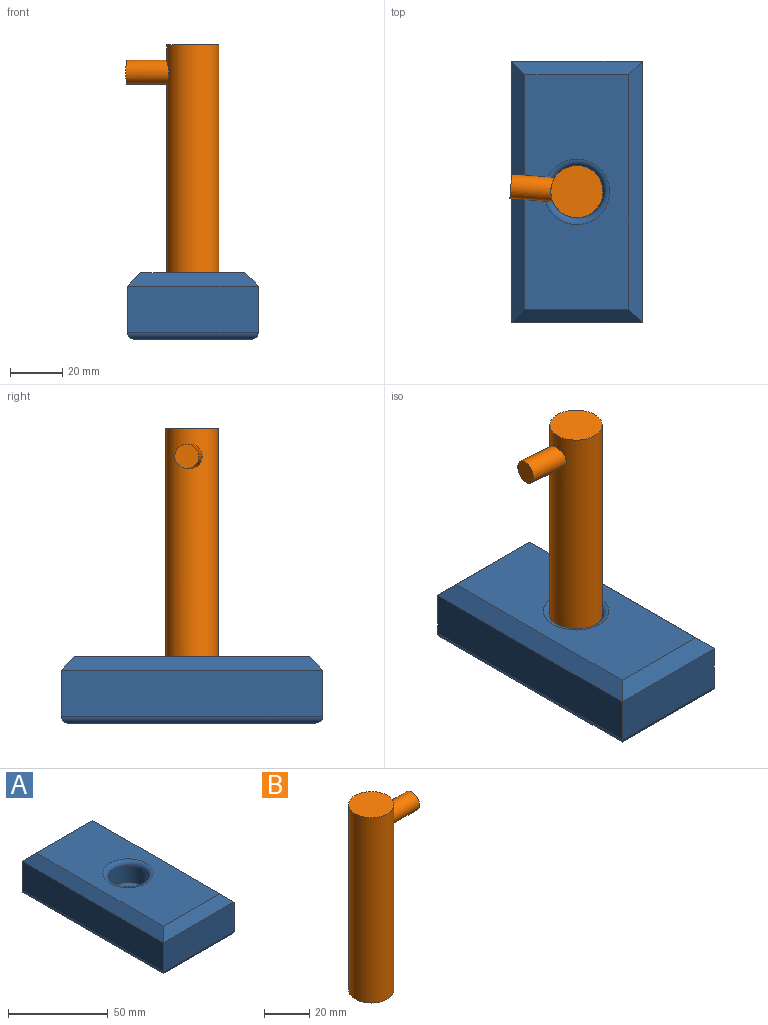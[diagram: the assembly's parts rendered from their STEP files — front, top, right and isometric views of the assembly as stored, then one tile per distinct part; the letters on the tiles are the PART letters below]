
ASSEMBLY  parts=2 mates=1
PART A: 17 faces, bbox 50x100x25.4 mm
  f0: plane 100x17.78mm, normal (1,0,0), area 1778mm2, adj f1,f3,f6,f13
  f1: plane 50x17.78mm, normal (0,1,0), area 889mm2, adj f0,f2,f8,f15
  f2: plane 100x17.78mm, normal (-1,0,0), area 1778mm2, adj f1,f3,f9,f16
  f3: plane 50x17.78mm, normal (0,-1,0), area 889mm2, adj f0,f2,f7,f14
  f4: plane 89.84x39.84mm, normal (0,0,1), area 3085.2mm2, adj f6,f7,f8,f9,f12
  f5: plane 94.92x44.92mm, normal (0,0,-1), area 4263.8mm2, adj f13,f14,f15,f16
  f6: plane 100x5.08mm, normal (0.71,0,0.71), area 681.9mm2, adj f0,f4,f7,f8
  f7: plane 50x5.08mm, normal (0,-0.71,0.71), area 322.7mm2, adj f3,f4,f6,f9
  f8: plane 50x5.08mm, normal (0,0.71,0.71), area 322.7mm2, adj f1,f4,f6,f9
  f9: plane 100x5.08mm, normal (-0.71,0,0.71), area 681.9mm2, adj f2,f4,f7,f8
  f10: cylinder r=10mm len=20mm, axis (0,0,1), area 638.4mm2, adj f11,f12
  f11: plane 20x20mm, normal (0,0,1), area 314.2mm2, adj f10
  f12: torus R=12.54mm, axis (0,0,1), area 273.8mm2, adj f4,f10
  f13: cylinder r=2.54mm len=100mm, axis (0,1,0), area 391.6mm2, adj f0,f5,f14,f15
  f14: cylinder r=2.54mm len=50mm, axis (1,0,0), area 192.1mm2, adj f3,f5,f13,f16
  f15: cylinder r=2.54mm len=50mm, axis (-1,0,0), area 192.1mm2, adj f1,f5,f13,f16
  f16: cylinder r=2.54mm len=100mm, axis (0,-1,0), area 391.6mm2, adj f2,f5,f14,f15
PART B: 5 faces, bbox 35.4x20x100 mm
  f0: cylinder r=10mm len=100mm, axis (0,0,-1), area 6214mm2, adj f1,f2,f3
  f1: plane 20x20mm, normal (0,0,1), area 314.2mm2, adj f0
  f2: plane 20x20mm, normal (0,0,-1), area 314.2mm2, adj f0
  f3: cylinder r=4.63mm len=16.54mm, axis (-1,0,0), area 464.1mm2, adj f0,f4
  f4: plane 9.26x9.26mm, normal (1,0,0), area 67.3mm2, adj f3
PLACE A t=(33.95,0,0)mm fixed
PLACE B rot(axis=(0,0,1),175.6deg) t=(33.95,0,12.7)mm
MATE revolute B.f0 <-> A.f10  axis (0,0,-1) through (33.95,0,12.7)mm
